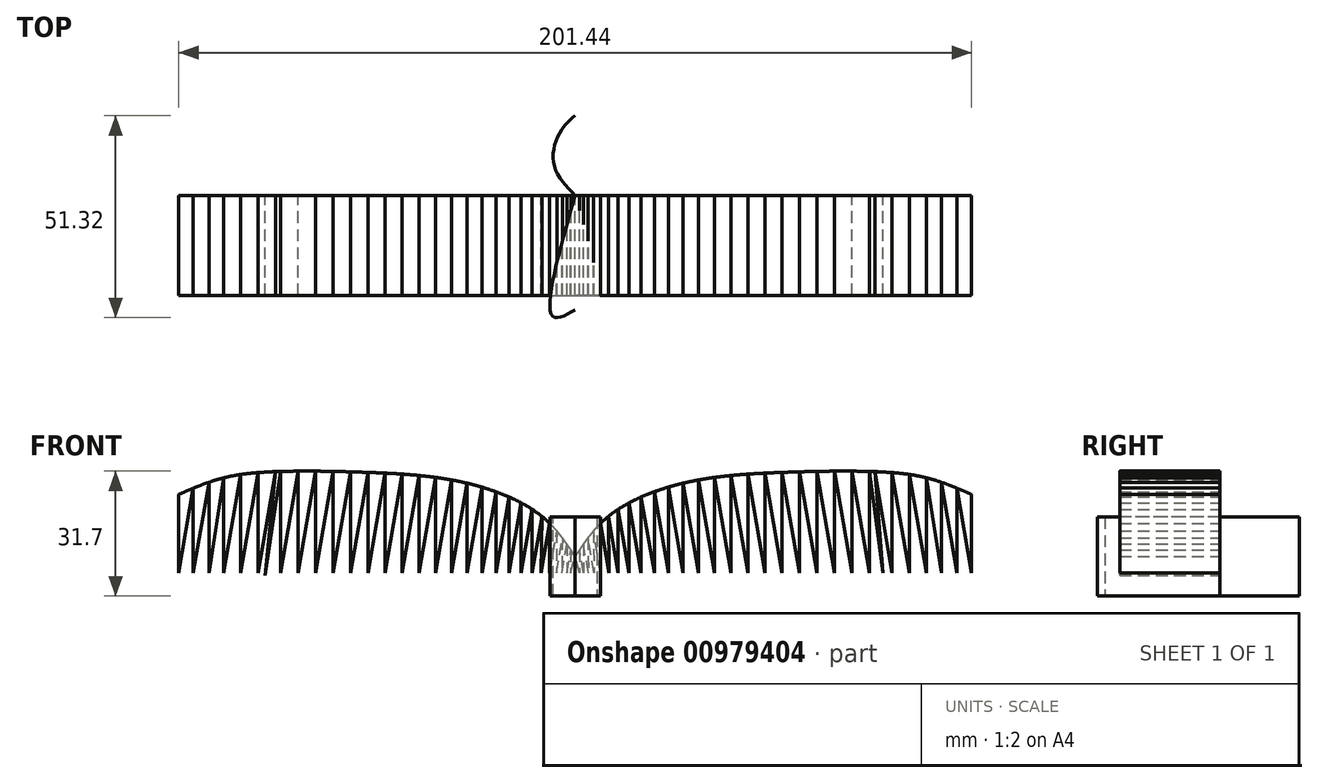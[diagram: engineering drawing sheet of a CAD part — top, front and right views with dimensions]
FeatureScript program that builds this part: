
annotation { "Feature Type Name" : "Feature", "Feature Type Description" : "" }
export const myFeature = defineFeature(function(context is Context, id is Id, definition is map)
    precondition{}
    {
        {
            var Q0;
            Q0=qCreatedBy(makeId("Front.planeOp"),FACE);
            var sketch = newSketch(context, id + "F0", { "sketchPlane" : qUnion([Q0])});
            skFitSpline(sketch, "E0", {"points": [v(0, 0) * mm, v(-8.64, 10.35) * mm, v(-28.14, 18.8) * mm, v(-53.68, 21.4) * mm, v(-74.78, 21.61) * mm, v(-89.26, 20) * mm, v(-100.72, 15.78) * mm], "startDerivative": vector(-49.5, 75.28) * mm, "endDerivative": vector(-80.54, -34.92) * mm});
            skLineSegment(sketch, "E1", {"start": v(-100.72, 15.78) * mm, "end": v(-100.72, -4.12) * mm});
            skLineSegment(sketch, "E2", {"start": v(-100.72, -4.12) * mm, "end": v(-97, 17.4) * mm});
            skLineSegment(sketch, "E3", {"start": v(-97, 17.4) * mm, "end": v(-97, -4.12) * mm});
            skLineSegment(sketch, "E4", {"start": v(-97, -4.12) * mm, "end": v(-93.03, 18.88) * mm});
            skLineSegment(sketch, "E5", {"start": v(-93.03, 18.88) * mm, "end": v(-93.03, -4.12) * mm});
            skLineSegment(sketch, "E6", {"start": v(-93.03, -4.12) * mm, "end": v(-89.26, 20) * mm});
            skLineSegment(sketch, "E7", {"start": v(-89.26, 20) * mm, "end": v(-89.26, -4.12) * mm});
            skLineSegment(sketch, "E8", {"start": v(-89.26, -4.12) * mm, "end": v(-84.95, 20.84) * mm});
            skLineSegment(sketch, "E9", {"start": v(-84.95, 20.84) * mm, "end": v(-84.95, -4.12) * mm});
            skLineSegment(sketch, "E10", {"start": v(-84.95, -4.12) * mm, "end": v(-80.55, 21.32) * mm});
            skLineSegment(sketch, "E11", {"start": v(-80.55, 21.32) * mm, "end": v(-80.55, -4.12) * mm});
            skLineSegment(sketch, "E12", {"start": v(-80.55, -4.12) * mm, "end": v(-76.1, 21.61) * mm});
            skLineSegment(sketch, "E13", {"start": v(-74.78, 21.61) * mm, "end": v(-74.78, -4.12) * mm});
            skLineSegment(sketch, "E14", {"start": v(-74.78, -4.12) * mm, "end": v(-70.34, 21.61) * mm});
            skLineSegment(sketch, "E15", {"start": v(-70.34, 21.61) * mm, "end": v(-70.34, -4.12) * mm});
            skLineSegment(sketch, "E16", {"start": v(-70.34, -4.12) * mm, "end": v(-65.88, 21.69) * mm});
            skLineSegment(sketch, "E17", {"start": v(-65.88, 21.69) * mm, "end": v(-65.88, -4.12) * mm});
            skLineSegment(sketch, "E18", {"start": v(-65.88, -4.12) * mm, "end": v(-61.44, 21.62) * mm});
            skLineSegment(sketch, "E19", {"start": v(-61.44, 21.62) * mm, "end": v(-61.44, -4.12) * mm});
            skLineSegment(sketch, "E20", {"start": v(-61.44, -4.12) * mm, "end": v(-57, 21.52) * mm});
            skLineSegment(sketch, "E21", {"start": v(-57, 21.52) * mm, "end": v(-57, -4.12) * mm});
            skLineSegment(sketch, "E22", {"start": v(-57, -4.12) * mm, "end": v(-52.6, 21.37) * mm});
            skLineSegment(sketch, "E23", {"start": v(-52.6, 21.37) * mm, "end": v(-52.6, -4.12) * mm});
            skLineSegment(sketch, "E24", {"start": v(-52.6, -4.12) * mm, "end": v(-48.24, 21.2) * mm});
            skLineSegment(sketch, "E25", {"start": v(-48.24, 21.2) * mm, "end": v(-48.24, -4.12) * mm});
            skLineSegment(sketch, "E26", {"start": v(-48.24, -4.12) * mm, "end": v(-43.9, 20.94) * mm});
            skLineSegment(sketch, "E27", {"start": v(-43.9, 20.94) * mm, "end": v(-43.9, -4.12) * mm});
            skLineSegment(sketch, "E28", {"start": v(-43.9, -4.12) * mm, "end": v(-39.64, 20.58) * mm});
            skLineSegment(sketch, "E29", {"start": v(-39.64, 20.58) * mm, "end": v(-39.64, -4.12) * mm});
            skLineSegment(sketch, "E30", {"start": v(-39.64, -4.12) * mm, "end": v(-35.46, 20.1) * mm});
            skLineSegment(sketch, "E31", {"start": v(-35.46, 20.1) * mm, "end": v(-35.46, -4.12) * mm});
            skLineSegment(sketch, "E32", {"start": v(-35.46, -4.12) * mm, "end": v(-31.39, 19.46) * mm});
            skLineSegment(sketch, "E33", {"start": v(-31.39, 19.46) * mm, "end": v(-31.39, -4.12) * mm});
            skLineSegment(sketch, "E34", {"start": v(-31.39, -4.12) * mm, "end": v(-27.43, 18.8) * mm});
            skLineSegment(sketch, "E35", {"start": v(-27.43, 18.8) * mm, "end": v(-27.43, -4.12) * mm});
            skLineSegment(sketch, "E36", {"start": v(-27.43, -4.12) * mm, "end": v(-23.67, 17.63) * mm});
            skLineSegment(sketch, "E37", {"start": v(-23.67, 17.63) * mm, "end": v(-23.67, -4.12) * mm});
            skLineSegment(sketch, "E38", {"start": v(-23.67, -4.12) * mm, "end": v(-20.12, 16.46) * mm});
            skLineSegment(sketch, "E39", {"start": v(-20.12, 16.46) * mm, "end": v(-20.12, -4.12) * mm});
            skLineSegment(sketch, "E40", {"start": v(-20.12, -4.12) * mm, "end": v(-16.8, 15.12) * mm});
            skLineSegment(sketch, "E41", {"start": v(-16.8, 15.12) * mm, "end": v(-16.8, -4.12) * mm});
            skLineSegment(sketch, "E42", {"start": v(-16.8, -4.12) * mm, "end": v(-13.73, 13.64) * mm});
            skLineSegment(sketch, "E43", {"start": v(-13.73, 13.64) * mm, "end": v(-13.73, -4.12) * mm});
            skLineSegment(sketch, "E44", {"start": v(-13.73, -4.12) * mm, "end": v(-10.94, 12) * mm});
            skLineSegment(sketch, "E45", {"start": v(-10.94, 12) * mm, "end": v(-10.94, -4.12) * mm});
            skLineSegment(sketch, "E46", {"start": v(-10.94, -4.12) * mm, "end": v(-8.47, 10.21) * mm});
            skLineSegment(sketch, "E47", {"start": v(-8.47, 10.21) * mm, "end": v(-8.64, -4.12) * mm});
            skLineSegment(sketch, "E48", {"start": v(-8.64, -4.12) * mm, "end": v(-6.48, 8.43) * mm});
            skLineSegment(sketch, "E49", {"start": v(-6.48, 8.43) * mm, "end": v(-6.48, -4.12) * mm});
            skLineSegment(sketch, "E50", {"start": v(-6.48, -4.12) * mm, "end": v(-4.65, 6.46) * mm});
            skLineSegment(sketch, "E51", {"start": v(-4.65, 6.46) * mm, "end": v(-4.78, -4.12) * mm});
            skLineSegment(sketch, "E52", {"start": v(-4.78, -4.12) * mm, "end": v(-3.25, 4.72) * mm});
            skLineSegment(sketch, "E53", {"start": v(-3.25, 4.72) * mm, "end": v(-3.36, -4.12) * mm});
            skLineSegment(sketch, "E54", {"start": v(-3.36, -4.12) * mm, "end": v(-2.1, 3.14) * mm});
            skLineSegment(sketch, "E55", {"start": v(-2.1, 3.14) * mm, "end": v(-2.1, -4.12) * mm});
            skLineSegment(sketch, "E56", {"start": v(-2.1, -4.12) * mm, "end": v(-1.1, 1.67) * mm});
            skLineSegment(sketch, "E57", {"start": v(-1.1, 1.67) * mm, "end": v(-1.18, -4.12) * mm});
            skLineSegment(sketch, "E58", {"start": v(-1.18, -4.12) * mm, "end": v(0, 0) * mm});
            skFitSpline(sketch, "E59.MirrorCS", {"points": [v(0, 0) * mm, v(8.64, 10.35) * mm, v(28.14, 18.8) * mm, v(53.68, 21.4) * mm, v(74.78, 21.61) * mm, v(89.26, 20) * mm, v(100.72, 15.78) * mm], "startDerivative": vector(49.5, 75.28) * mm, "endDerivative": vector(80.54, -34.92) * mm});
            skLineSegment(sketch, "E60.MirrorCS", {"start": v(100.72, 15.78) * mm, "end": v(100.72, -4.12) * mm});
            skLineSegment(sketch, "E61.MirrorCS", {"start": v(100.72, -4.12) * mm, "end": v(97, 17.4) * mm});
            skLineSegment(sketch, "E62.MirrorCS", {"start": v(97, 17.4) * mm, "end": v(97, -4.12) * mm});
            skLineSegment(sketch, "E63.MirrorCS", {"start": v(97, -4.12) * mm, "end": v(93.03, 18.88) * mm});
            skLineSegment(sketch, "E64.MirrorCS", {"start": v(93.03, 18.88) * mm, "end": v(93.03, -4.12) * mm});
            skLineSegment(sketch, "E65.MirrorCS", {"start": v(93.03, -4.12) * mm, "end": v(89.26, 20) * mm});
            skLineSegment(sketch, "E66.MirrorCS", {"start": v(89.26, 20) * mm, "end": v(89.26, -4.12) * mm});
            skLineSegment(sketch, "E67.MirrorCS", {"start": v(89.26, -4.12) * mm, "end": v(84.95, 20.84) * mm});
            skLineSegment(sketch, "E68.MirrorCS", {"start": v(84.95, 20.84) * mm, "end": v(84.95, -4.12) * mm});
            skLineSegment(sketch, "E69.MirrorCS", {"start": v(84.95, -4.12) * mm, "end": v(80.55, 21.32) * mm});
            skLineSegment(sketch, "E70.MirrorCS", {"start": v(80.55, 21.32) * mm, "end": v(80.55, -4.12) * mm});
            skLineSegment(sketch, "E71.MirrorCS", {"start": v(80.55, -4.12) * mm, "end": v(76.1, 21.61) * mm});
            skLineSegment(sketch, "E72.MirrorCS", {"start": v(74.78, 21.61) * mm, "end": v(74.78, -4.12) * mm});
            skLineSegment(sketch, "E73.MirrorCS", {"start": v(74.78, -4.12) * mm, "end": v(70.34, 21.61) * mm});
            skLineSegment(sketch, "E74.MirrorCS", {"start": v(70.34, 21.61) * mm, "end": v(70.34, -4.12) * mm});
            skLineSegment(sketch, "E75.MirrorCS", {"start": v(70.34, -4.12) * mm, "end": v(65.88, 21.69) * mm});
            skLineSegment(sketch, "E76.MirrorCS", {"start": v(65.88, 21.69) * mm, "end": v(65.88, -4.12) * mm});
            skLineSegment(sketch, "E77.MirrorCS", {"start": v(65.88, -4.12) * mm, "end": v(61.44, 21.62) * mm});
            skLineSegment(sketch, "E78.MirrorCS", {"start": v(61.44, 21.62) * mm, "end": v(61.44, -4.12) * mm});
            skLineSegment(sketch, "E79.MirrorCS", {"start": v(61.44, -4.12) * mm, "end": v(57, 21.52) * mm});
            skLineSegment(sketch, "E80.MirrorCS", {"start": v(57, 21.52) * mm, "end": v(57, -4.12) * mm});
            skLineSegment(sketch, "E81.MirrorCS", {"start": v(57, -4.12) * mm, "end": v(52.6, 21.37) * mm});
            skLineSegment(sketch, "E82.MirrorCS", {"start": v(52.6, 21.37) * mm, "end": v(52.6, -4.12) * mm});
            skLineSegment(sketch, "E83.MirrorCS", {"start": v(52.6, -4.12) * mm, "end": v(48.24, 21.2) * mm});
            skLineSegment(sketch, "E84.MirrorCS", {"start": v(48.24, 21.2) * mm, "end": v(48.24, -4.12) * mm});
            skLineSegment(sketch, "E85.MirrorCS", {"start": v(48.24, -4.12) * mm, "end": v(43.9, 20.94) * mm});
            skLineSegment(sketch, "E86.MirrorCS", {"start": v(43.9, 20.94) * mm, "end": v(43.9, -4.12) * mm});
            skLineSegment(sketch, "E87.MirrorCS", {"start": v(43.9, -4.12) * mm, "end": v(39.64, 20.58) * mm});
            skLineSegment(sketch, "E88.MirrorCS", {"start": v(39.64, 20.58) * mm, "end": v(39.64, -4.12) * mm});
            skLineSegment(sketch, "E89.MirrorCS", {"start": v(39.64, -4.12) * mm, "end": v(35.46, 20.1) * mm});
            skLineSegment(sketch, "E90.MirrorCS", {"start": v(35.46, 20.1) * mm, "end": v(35.46, -4.12) * mm});
            skLineSegment(sketch, "E91.MirrorCS", {"start": v(35.46, -4.12) * mm, "end": v(31.39, 19.46) * mm});
            skLineSegment(sketch, "E92.MirrorCS", {"start": v(31.39, 19.46) * mm, "end": v(31.39, -4.12) * mm});
            skLineSegment(sketch, "E93.MirrorCS", {"start": v(31.39, -4.12) * mm, "end": v(27.43, 18.8) * mm});
            skLineSegment(sketch, "E94.MirrorCS", {"start": v(27.43, 18.8) * mm, "end": v(27.43, -4.12) * mm});
            skLineSegment(sketch, "E95.MirrorCS", {"start": v(27.43, -4.12) * mm, "end": v(23.67, 17.63) * mm});
            skLineSegment(sketch, "E96.MirrorCS", {"start": v(23.67, 17.63) * mm, "end": v(23.67, -4.12) * mm});
            skLineSegment(sketch, "E97.MirrorCS", {"start": v(23.67, -4.12) * mm, "end": v(20.12, 16.46) * mm});
            skLineSegment(sketch, "E98.MirrorCS", {"start": v(20.12, 16.46) * mm, "end": v(20.12, -4.12) * mm});
            skLineSegment(sketch, "E99.MirrorCS", {"start": v(20.12, -4.12) * mm, "end": v(16.8, 15.12) * mm});
            skLineSegment(sketch, "E100.MirrorCS", {"start": v(16.8, 15.12) * mm, "end": v(16.8, -4.12) * mm});
            skLineSegment(sketch, "E101.MirrorCS", {"start": v(16.8, -4.12) * mm, "end": v(13.73, 13.64) * mm});
            skLineSegment(sketch, "E102.MirrorCS", {"start": v(13.73, 13.64) * mm, "end": v(13.73, -4.12) * mm});
            skLineSegment(sketch, "E103.MirrorCS", {"start": v(13.73, -4.12) * mm, "end": v(10.94, 12) * mm});
            skLineSegment(sketch, "E104.MirrorCS", {"start": v(10.94, 12) * mm, "end": v(10.94, -4.12) * mm});
            skLineSegment(sketch, "E105.MirrorCS", {"start": v(10.94, -4.12) * mm, "end": v(8.47, 10.21) * mm});
            skLineSegment(sketch, "E106.MirrorCS", {"start": v(8.47, 10.21) * mm, "end": v(8.64, -4.12) * mm});
            skLineSegment(sketch, "E107.MirrorCS", {"start": v(8.64, -4.12) * mm, "end": v(6.48, 8.43) * mm});
            skLineSegment(sketch, "E108.MirrorCS", {"start": v(6.48, 8.43) * mm, "end": v(6.48, -4.12) * mm});
            skLineSegment(sketch, "E109.MirrorCS", {"start": v(6.48, -4.12) * mm, "end": v(4.65, 6.46) * mm});
            skLineSegment(sketch, "E110.MirrorCS", {"start": v(4.65, 6.46) * mm, "end": v(4.78, -4.12) * mm});
            skLineSegment(sketch, "E111.MirrorCS", {"start": v(4.78, -4.12) * mm, "end": v(3.25, 4.72) * mm});
            skLineSegment(sketch, "E112.MirrorCS", {"start": v(3.25, 4.72) * mm, "end": v(3.36, -4.12) * mm});
            skLineSegment(sketch, "E113.MirrorCS", {"start": v(3.36, -4.12) * mm, "end": v(2.1, 3.14) * mm});
            skLineSegment(sketch, "E114.MirrorCS", {"start": v(1.1, 1.67) * mm, "end": v(1.18, -4.12) * mm});
            skLineSegment(sketch, "E115.MirrorCS", {"start": v(1.18, -4.12) * mm, "end": v(0, 0) * mm});
            skLineSegment(sketch, "E116.MirrorCS", {"start": v(2.1, 3.14) * mm, "end": v(2.1, -4.12) * mm});
            skLineSegment(sketch, "E117.MirrorCS", {"start": v(2.1, -4.12) * mm, "end": v(1.1, 1.67) * mm});
            skLineSegment(sketch, "E118", {"start": v(-76.1, 21.61) * mm, "end": v(-78.71, -4.8) * mm});
            skLineSegment(sketch, "E119", {"start": v(-78.71, -4.8) * mm, "end": v(-74.78, 21.61) * mm});
            skLineSegment(sketch, "E120", {"start": v(76.1, 21.61) * mm, "end": v(78.16, -4.12) * mm});
            skLineSegment(sketch, "E121", {"start": v(78.16, -4.12) * mm, "end": v(74.78, 21.61) * mm});
            skSolve(sketch);
        }
        {
            var Q0;
            Q0=qSketchRegion(id+"F0",true);
            extrude(context, id + "F1", {"entities" : qUnion([Q0]), "depth" : 25.4 * mm, "offsetDistance" : 25.4 * mm});
        }
        {
            var Q0;
            Q0=qCreatedBy(makeId("Top.planeOp"),FACE);
            var sketch = newSketch(context, id + "F2", { "sketchPlane" : qUnion([Q0])});
            skLineSegment(sketch, "E122.left", {"start": v(-6.44, 14.6) * mm, "end": v(-6.44, 14.6) * mm});
            skLineSegment(sketch, "E122.right", {"start": v(-5.43, 14.6) * mm, "end": v(-5.43, 14.6) * mm});
            skLineSegment(sketch, "E123", {"start": v(0, 0) * mm, "end": v(0, 20.29) * mm});
            skFitSpline(sketch, "E124", {"points": [v(0, 0) * mm, v(-5.43, 8.01) * mm, v(-3.71, 16.29) * mm, v(0, 20.29) * mm], "startDerivative": vector(-19.34, 20.16) * mm, "endDerivative": vector(14.14, 11.9) * mm});
            skFitSpline(sketch, "E125.MirrorCS", {"points": [v(0, 0) * mm, v(5.43, 8.01) * mm, v(3.71, 16.29) * mm, v(0, 20.29) * mm], "startDerivative": vector(19.34, 20.16) * mm, "endDerivative": vector(-14.14, 11.9) * mm});
            skLineSegment(sketch, "E126", {"start": v(0, 0) * mm, "end": v(0, -29.12) * mm});
            skFitSpline(sketch, "E127", {"points": [v(0, 0) * mm, v(-5.7, -30.68) * mm, v(0, -29.12) * mm], "startDerivative": vector(-17.55, -61.15) * mm, "endDerivative": vector(22.86, 12.58) * mm});
            skFitSpline(sketch, "E128.MirrorCS", {"points": [v(0, 0) * mm, v(5.7, -30.68) * mm, v(0, -29.12) * mm], "startDerivative": vector(17.55, -61.15) * mm, "endDerivative": vector(-22.86, 12.58) * mm});
            skSolve(sketch);
        }
        {
            var Q0;
            Q0=qSketchRegion(id+"F2",true);
            extrude(context, id + "F3", {"entities" : qUnion([Q0]), "depth" : 10 * mm, "offsetDistance" : 25.4 * mm, "hasSecondDirection" : true, "secondDirectionOppositeDirection" : true, "secondDirectionDepth" : 10 * mm});
        }
    });
